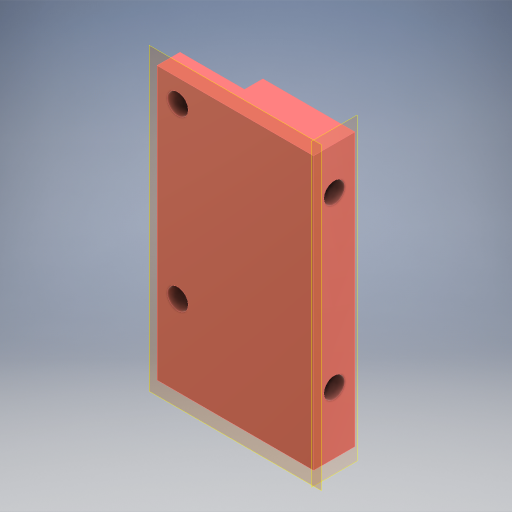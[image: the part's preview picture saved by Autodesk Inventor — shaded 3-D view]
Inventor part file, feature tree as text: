
AUTODESK INVENTOR PART (.ipt)
format: ipt  version: 2024 (Build 280153000, 153)  size: 288,256 bytes
history: native  units: in
note: dims shown in document units (in); Inventor stores cm internally (conversion verified against a paired STEP export)
features: other x5, extrude x3, sketch x3, reference x3
ambient origin geometry x8: Origin, YZ Plane, XZ Plane, XY Plane, X Axis, Y Axis, Z Axis, Center Point
bodies: Body1 (feature_tree)
feature tree (14):
  other  "솔리드1"
  other  "작업 평면1"
  extrude  "돌출1"  Depth=0.1181in TaperAngle=0.0deg
  other  "작업 평면2"
  extrude  "돌출2"  Depth=0.4724in TaperAngle=0.0deg
  extrude  "돌출3"  Depth=0.4724in TaperAngle=0.0deg
  sketch  "스케치1"
  reference  "참조1"
  sketch  "스케치2"
  reference  "참조2"
  sketch  "스케치3"
  reference  "참조3"
  other  "조립품9"
  other  "foot_right_connection_MIR:1"
